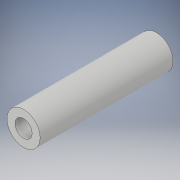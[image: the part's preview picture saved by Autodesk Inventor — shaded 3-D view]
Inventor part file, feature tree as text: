
AUTODESK INVENTOR PART (.ipt)
format: ipt  version: 2017 (Build 210142000, 142)  size: 92,672 bytes
history: native  units: in
note: dims shown in document units (in); Inventor stores cm internally (conversion verified against a paired STEP export)
features: extrude x1, sketch x1
ambient origin geometry x8: Origin, YZ Plane, XZ Plane, XY Plane, X Axis, Y Axis, Z Axis, Center Point
bodies: Solid1 (feature_tree)
feature tree (2):
  extrude  "Extrusion1"  [1 undecoded]
  sketch  "Sketch1"  dims[d0=2.0in d1=0.0in]
note: 1 required parameter value undecoded (feature->parameter linkage not recoverable at this tier; creation-order binding heuristic only, values carry confidence <= 0.55)
